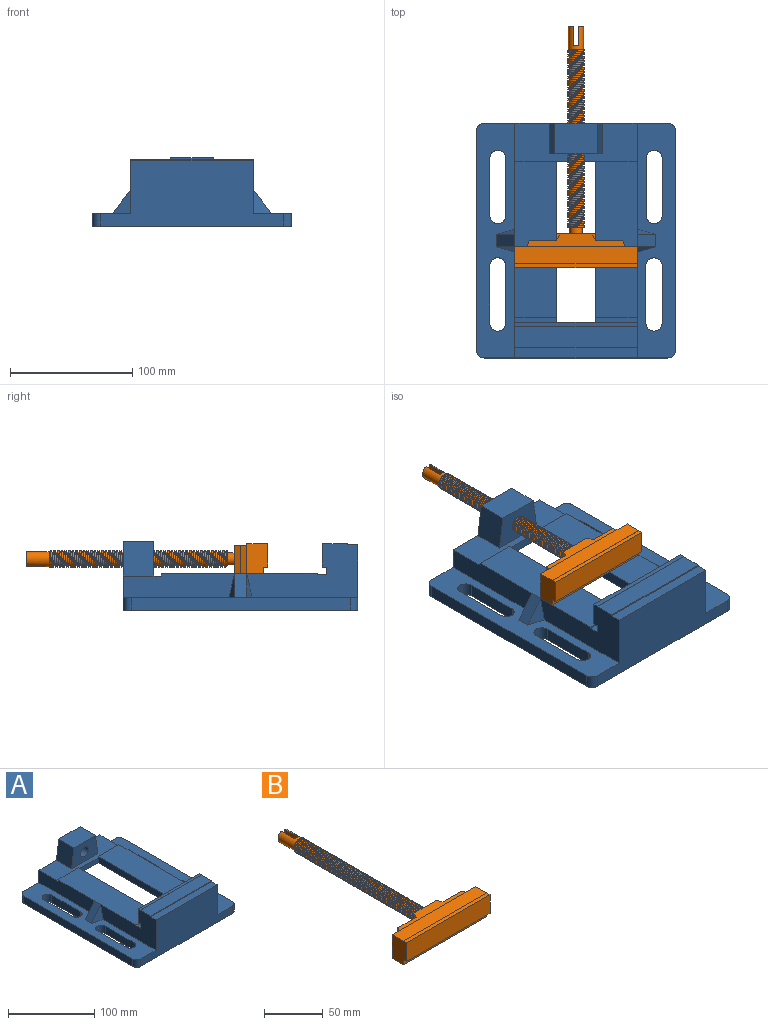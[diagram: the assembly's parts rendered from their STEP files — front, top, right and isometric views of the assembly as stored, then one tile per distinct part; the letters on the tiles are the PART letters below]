
ASSEMBLY  parts=2 mates=1
PART A: 67 faces, bbox 163x192x56 mm
  f0: plane 91x19.5mm, normal (-1,0,0), area 1670.3mm2, adj f1,f9,f10,f16,f17,f64
  f1: plane 192x31.5mm, normal (0,0,1), area 4328.3mm2, adj f0,f14,f17,f18,f21,f22,f23,f24
  f2: plane 91x19.5mm, normal (1,0,0), area 1670.3mm2, adj f3,f15,f16,f17,f41,f61
  f3: plane 192x31.5mm, normal (0,0,1), area 4310.1mm2, adj f2,f13,f14,f17,f19,f20,f27,f28
  f4: plane 192x163mm, normal (0,0,-1), area 14508.2mm2, adj f14,f17,f19,f20,f21,f22,f23,f24
  f5: plane 100x14.3mm, normal (0,1,0), area 886mm2, adj f7,f8,f12,f13,f18,f50,f53,f59
  f6: plane 32x7mm, normal (0,-1,0), area 224mm2, adj f7,f8,f16,f59
  f7: plane 135.5x9mm, normal (1,0,0), area 1212mm2, adj f5,f6,f9,f10,f11,f12,f59
  f8: plane 135.5x9mm, normal (-1,0,0), area 1212mm2, adj f5,f6,f15,f41,f49,f50,f59
  f9: plane 128x34mm, normal (0,0,1), area 4352mm2, adj f0,f7,f10,f11,f18,f66
  f10: plane 34x2mm, normal (0,1,0), area 68mm2, adj f0,f7,f9,f16
  f11: plane 34x1mm, normal (0,-1,0), area 34mm2, adj f7,f9,f12,f18
  f12: plane 34x7.5mm, normal (0,0,1), area 255mm2, adj f5,f7,f11,f18
  f13: plane 91x44.1mm, normal (1,0,0), area 2413.4mm2, adj f3,f5,f14,f15,f46,f47,f48,f49
  f14: plane 150.3x53.5mm, normal (0,-1,0), area 5878.1mm2, adj f1,f3,f4,f13,f18,f23,f40,f48
  f15: plane 128x34mm, normal (0,0,1), area 4352mm2, adj f2,f8,f13,f41,f49,f65
  f16: plane 100x31mm, normal (0,0,1), area 2025mm2, adj f0,f2,f6,f10,f17,f41,f42,f43
  f17: plane 150.3x56mm, normal (0,1,0), area 4278.8mm2, adj f0,f1,f2,f3,f4,f16,f20,f21
  f18: plane 91x44.1mm, normal (-1,0,0), area 2413.4mm2, adj f1,f5,f9,f11,f12,f14,f46,f47
  f19: plane 179.3x10.5mm, normal (1,0,0), area 1882.7mm2, adj f3,f4,f20,f40
  f20: cylinder r=6.35mm len=10.5mm, axis (0,0,-1), area 104.7mm2, adj f3,f4,f17,f19
  f21: cylinder r=6.35mm len=10.5mm, axis (0,0,-1), area 104.7mm2, adj f1,f4,f17,f22
  f22: plane 179.3x10.5mm, normal (-1,0,0), area 1882.7mm2, adj f1,f4,f21,f23
  f23: cylinder r=6.35mm len=10.5mm, axis (0,0,-1), area 104.7mm2, adj f1,f4,f14,f22
  f24: cylinder r=6.5mm len=13mm, axis (0,0,-1), area 214.4mm2, adj f1,f4,f25,f36
  f25: plane 47x10.5mm, normal (-1,0,0), area 493.5mm2, adj f1,f4,f24,f26
  f26: cylinder r=6.5mm len=13mm, axis (0,0,-1), area 214.4mm2, adj f1,f4,f25,f36
  f27: cylinder r=6.67mm len=13.34mm, axis (0,0,-1), area 219.9mm2, adj f3,f4,f28,f37
  f28: plane 46.66x10.5mm, normal (-1,0,0), area 490mm2, adj f3,f4,f27,f29
  f29: cylinder r=6.67mm len=13.34mm, axis (0,0,-1), area 219.9mm2, adj f3,f4,f28,f37
  f30: cylinder r=6.5mm len=13mm, axis (0,0,-1), area 214.4mm2, adj f3,f4,f31,f38
  f31: plane 47x10.5mm, normal (-1,0,0), area 493.5mm2, adj f3,f4,f30,f32
  f32: cylinder r=6.5mm len=13mm, axis (0,0,-1), area 214.4mm2, adj f3,f4,f31,f38
  f33: cylinder r=6.5mm len=13mm, axis (0,0,-1), area 214.4mm2, adj f1,f4,f34,f39
  f34: plane 47x10.5mm, normal (-1,0,0), area 493.5mm2, adj f1,f4,f33,f35
  f35: cylinder r=6.5mm len=13mm, axis (0,0,-1), area 214.4mm2, adj f1,f4,f34,f39
  f36: plane 47x10.5mm, normal (1,0,0), area 493.5mm2, adj f1,f4,f24,f26
  f37: plane 46.66x10.5mm, normal (1,0,0), area 490mm2, adj f3,f4,f27,f29
  f38: plane 47x10.5mm, normal (1,0,0), area 493.5mm2, adj f3,f4,f30,f32
  f39: plane 47x10.5mm, normal (1,0,0), area 493.5mm2, adj f1,f4,f33,f35
  f40: cylinder r=6.35mm len=10.5mm, axis (0,0,-1), area 104.7mm2, adj f3,f4,f14,f19
  f41: plane 34x2mm, normal (0,1,0), area 68mm2, adj f2,f8,f15,f16
  f42: plane 28x25mm, normal (-0.99,0,0.14), area 706.9mm2, adj f16,f17,f43,f45
  f43: plane 43x28mm, normal (0,-1,0), area 950.7mm2, adj f16,f42,f44,f45,f60
  f44: plane 28x25mm, normal (0.99,0,0.14), area 706.9mm2, adj f16,f17,f43,f45
  f45: plane 35.13x25mm, normal (0,0,1), area 878.2mm2, adj f17,f42,f43,f44
  f46: plane 100x17mm, normal (0,0,1), area 1700mm2, adj f13,f18,f47,f51
  f47: plane 100x1mm, normal (0,-1,0), area 100mm2, adj f13,f18,f46,f48
  f48: plane 100x8.5mm, normal (0,0,1), area 850mm2, adj f13,f14,f18,f47
  f49: plane 34x1mm, normal (0,-1,0), area 34mm2, adj f8,f13,f15,f50
  f50: plane 34x7.5mm, normal (0,0,1), area 255mm2, adj f5,f8,f13,f49
  f51: plane 100x0.1mm, normal (0,-1,0), area 10mm2, adj f13,f18,f46,f52
  f52: plane 100x3.75mm, normal (0,0,1), area 375mm2, adj f13,f18,f51,f54
  f53: plane 100x3.75mm, normal (0,0,-1), area 375mm2, adj f5,f13,f18,f54
  f54: plane 100x19.3mm, normal (0,1,0), area 1930mm2, adj f13,f18,f52,f53
  f55: plane 80x21mm, normal (0,1,0), area 1680mm2, adj f4,f56,f58,f59
  f56: plane 172x21mm, normal (1,0,0), area 3612mm2, adj f4,f55,f57,f59
  f57: plane 80x21mm, normal (0,-1,0), area 1680mm2, adj f4,f56,f58,f59
  f58: plane 172x21mm, normal (-1,0,0), area 3612mm2, adj f4,f55,f57,f59
  f59: plane 172x80mm, normal (0,0,-1), area 9424mm2, adj f5,f6,f7,f8,f55,f56,f57,f58
  f60: cylinder r=6.75mm len=25mm, axis (0,1,0), area 1060.3mm2, adj f17,f43
  f61: plane 19.5x15mm, normal (0.27,0.94,0.21), area 155.6mm2, adj f2,f3,f65
  f62: plane 19.5x15mm, normal (0.27,-0.94,0.21), area 155.6mm2, adj f3,f13,f65
  f63: plane 19.5x15mm, normal (-0.27,-0.94,0.21), area 155.6mm2, adj f1,f18,f66
  f64: plane 19.5x15mm, normal (-0.27,0.94,0.21), area 155.6mm2, adj f0,f1,f66
  f65: plane 19.5x15mm, normal (0.79,0,0.61), area 246mm2, adj f3,f15,f61,f62
  f66: plane 19.5x15mm, normal (-0.79,0,0.61), area 246mm2, adj f1,f9,f63,f64
PART B: 39 faces, bbox 100.1x198.1x34.7 mm
  f0: plane 11.67x4.2mm, normal (0,1,0), area 35.8mm2, adj f34,f38
  f1: plane 12.86x8.87mm, normal (0,1,0), area 13.6mm2, adj f28,f29,f32,f34
  f2: cylinder r=5mm len=10mm, axis (0,-1,0), area 177.5mm2, adj f22,f27
  f3: plane 23.25x5.5mm, normal (0.91,0.42,0), area 141.1mm2, adj f17,f18,f22,f23
  f4: plane 23.25x22.18mm, normal (0,1,0), area 515.7mm2, adj f13,f16,f17,f20
  f5: plane 100x24.5mm, normal (0,1,0), area 590mm2, adj f7,f9,f13,f14,f15,f16,f17
  f6: plane 100x3.8mm, normal (0,0,1), area 380mm2, adj f7,f9,f10,f11
  f7: plane 24.6x17.3mm, normal (1,0,0), area 404.1mm2, adj f5,f6,f8,f10,f11,f12,f13,f14
  f8: plane 100x3.8mm, normal (0,0,-1), area 380mm2, adj f7,f9,f11,f12
  f9: plane 24.6x17.3mm, normal (-1,0,0), area 404.1mm2, adj f5,f6,f8,f10,f11,f12,f13,f14
  f10: plane 100x0.1mm, normal (0,1,0), area 10mm2, adj f6,f7,f9,f14
  f11: plane 100x19.3mm, normal (0,-1,0), area 1930mm2, adj f6,f7,f8,f9
  f12: plane 100x5.3mm, normal (0,-1,0), area 530mm2, adj f7,f8,f9,f13
  f13: plane 100x18.5mm, normal (0,0,-1), area 1740.9mm2, adj f4,f5,f7,f9,f12,f15,f16,f18
  f14: plane 100x13.5mm, normal (0,0,1), area 1350mm2, adj f5,f7,f9,f10
  f15: plane 23.25x5mm, normal (0.94,0.34,0), area 123.7mm2, adj f5,f13,f17,f18
  f16: plane 23.25x5mm, normal (-0.94,0.34,0), area 123.7mm2, adj f4,f5,f13,f17
  f17: plane 80x10.5mm, normal (0,0,1), area 552.8mm2, adj f3,f4,f5,f15,f16,f18,f20,f22
  f18: plane 23.25x22.18mm, normal (0,1,0), area 515.7mm2, adj f3,f13,f15,f17
  f19: plane 32x10mm, normal (0,-1,0), area 320mm2, adj f13,f21,f24,f26
  f20: plane 23.25x5.5mm, normal (-0.91,0.42,0), area 141.1mm2, adj f4,f17,f22,f25
  f21: plane 32x5.5mm, normal (0,0,-1), area 176mm2, adj f19,f22,f24,f26
  f22: plane 33.25x32mm, normal (0,1,0), area 866.2mm2, adj f2,f3,f17,f20,f21,f23,f24,f25
  f23: plane 5.5x2.56mm, normal (0,0,1), area 7.1mm2, adj f3,f22,f24
  f24: plane 10x5.5mm, normal (1,0,0), area 55mm2, adj f19,f21,f22,f23
  f25: plane 5.5x2.56mm, normal (0,0,1), area 7.1mm2, adj f20,f22,f26
  f26: plane 10x5.5mm, normal (-1,0,0), area 55mm2, adj f19,f21,f22,f25
  f27: plane 13.9x12.55mm, normal (0,-1,0), area 46.1mm2, adj f2,f28,f29,f30,f31,f32
  f28: bspline ~146.78x15.88mm, area 2613.8mm2, adj f1,f27,f30,f32,f33
  f29: bspline ~146.28x15.88mm, area 2611.2mm2, adj f1,f27,f30,f31,f32,f33
  f30: cylinder r=5.53mm len=145.5mm, axis (0,-1,0), area 4008mm2, adj f27,f28,f29,f33
  f31: plane 1.34x0.28mm, normal (0,0,-1), area 0.2mm2, adj f27,f29,f32
  f32: cylinder r=6.88mm len=145.5mm, axis (0,-1,0), area 2005.7mm2, adj f1,f27,f28,f29,f31
  f33: plane 12.02x7.86mm, normal (0,-1,0), area 10.3mm2, adj f28,f29,f30,f34
  f34: cylinder r=6.15mm len=19mm, axis (0,-1,0), area 607mm2, adj f0,f1,f33,f35,f36,f37,f38
  f35: plane 11.67x4.2mm, normal (0,1,0), area 35.8mm2, adj f34,f37
  f36: plane 12.3x3.9mm, normal (0,1,0), area 47.2mm2, adj f34,f37,f38
  f37: plane 16.03x11.67mm, normal (1,0,0), area 187mm2, adj f34,f35,f36
  f38: plane 16.03x11.67mm, normal (-1,0,0), area 187mm2, adj f0,f34,f36
PLACE A t=(-2.65,-58.61,31.84)mm fixed
PLACE B t=(-2.65,-14.26,31.84)mm
MATE slider B.f2 <-> A.f60  axis (0,-1,0) through (78.85,203.44,73.7)mm
